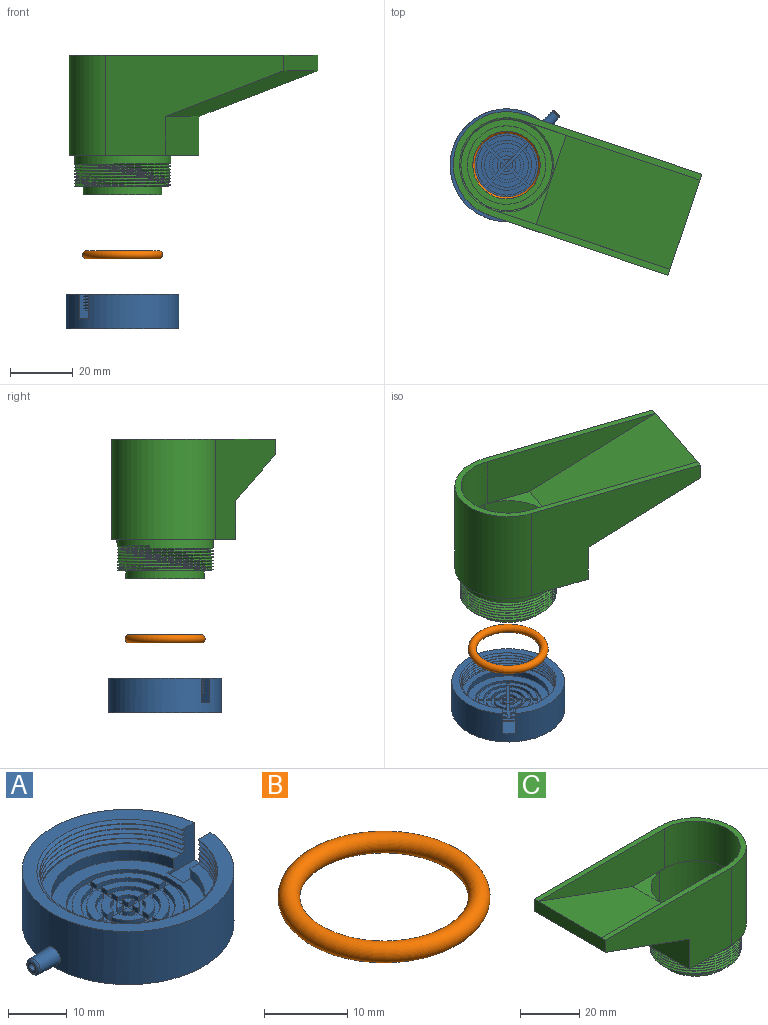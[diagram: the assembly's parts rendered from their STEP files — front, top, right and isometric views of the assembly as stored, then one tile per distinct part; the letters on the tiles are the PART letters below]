
ASSEMBLY  parts=3 mates=2
PART A: 117 faces, bbox 41.6x37.1x12.2 mm
  f0: cylinder r=18mm len=36mm, axis (0,0,1), area 1204.3mm2, adj f19,f69,f106,f113,f114,f115
  f1: cylinder r=15mm len=30mm, axis (0,0,1), area 16.3mm2, adj f16,f17,f20,f70,f113,f114
  f2: cylinder r=15mm len=30mm, axis (0,0,1), area 9mm2, adj f11,f15,f113,f114
  f3: cylinder r=15mm len=30mm, axis (0,0,1), area 9mm2, adj f10,f14,f113,f114
  f4: cylinder r=15mm len=30mm, axis (0,0,1), area 9mm2, adj f9,f13,f113,f114
  f5: cylinder r=15mm len=30mm, axis (0,0,1), area 9mm2, adj f8,f12,f113,f114
  f6: cylinder r=15mm len=6.76mm, axis (0,0,1), area 0.3mm2, adj f7,f19,f113
  f7: bspline ~31.89x31.56mm, area 26.7mm2, adj f6,f12,f19,f113
  f8: bspline ~36.44x31.56mm, area 83.4mm2, adj f5,f13,f113,f114
  f9: bspline ~36.44x31.56mm, area 83.4mm2, adj f4,f14,f113,f114
  f10: bspline ~36.44x31.56mm, area 83.4mm2, adj f3,f15,f113,f114
  f11: bspline ~36.44x31.56mm, area 83.4mm2, adj f2,f16,f113,f114
  f12: bspline ~36.44x31.56mm, area 65.4mm2, adj f5,f7,f19,f113,f114
  f13: bspline ~36.44x31.56mm, area 83.4mm2, adj f4,f8,f113,f114
  f14: bspline ~36.44x31.56mm, area 83.4mm2, adj f3,f9,f113,f114
  f15: bspline ~36.44x31.56mm, area 83.4mm2, adj f2,f10,f113,f114
  f16: bspline ~36.44x31.56mm, area 83.4mm2, adj f1,f11,f113,f114
  f17: plane 30x29.87mm, normal (0,0,1), area 167.9mm2, adj f1,f18,f71,f113,f114
  f18: cone r=13mm half-angle=5deg, axis (0,0,-1), area 172.9mm2, adj f17,f72,f113,f114
  f19: plane 36.65x36.53mm, normal (0,0,1), area 265.4mm2, adj f0,f6,f7,f12,f113,f114
  f20: bspline ~31.89x31.56mm, area 41.7mm2, adj f1,f21,f70,f114
  f21: bspline ~31.56x18.22mm, area 41.7mm2, adj f20,f70,f71,f114
  f22: cylinder r=18mm len=0.17mm, axis (0,0,1), area 0mm2, adj f95,f101,f111
  f23: cylinder r=18mm len=0.17mm, axis (0,0,1), area 0mm2, adj f96,f101,f111
  f24: cylinder r=18mm len=0.17mm, axis (0,0,1), area 0mm2, adj f96,f102,f111
  f25: plane 21x20.99mm, normal (0,0,1), area 171mm2, adj f26,f27,f28,f29,f34,f35,f36,f37
  f26: cylinder r=9.5mm len=8.99mm, axis (0,0,-1), area 13.9mm2, adj f25,f30,f94,f99
  f27: cylinder r=9.5mm len=8.99mm, axis (0,0,-1), area 13.9mm2, adj f25,f31,f95,f98
  f28: cylinder r=9.5mm len=8.99mm, axis (0,0,-1), area 13.9mm2, adj f25,f32,f93,f96
  f29: cylinder r=9.5mm len=8.99mm, axis (0,0,-1), area 13.9mm2, adj f25,f33,f97,f100
  f30: plane 8.99x8.99mm, normal (0,0,1), area 19.1mm2, adj f26,f34,f94,f99
  f31: plane 8.99x8.99mm, normal (0,0,1), area 19.1mm2, adj f27,f35,f95,f98
  f32: plane 8.99x8.99mm, normal (0,0,1), area 19.1mm2, adj f28,f36,f93,f96
  f33: plane 8.99x8.99mm, normal (0,0,1), area 19.1mm2, adj f29,f37,f97,f100
  f34: cylinder r=8mm len=7.48mm, axis (0,0,-1), area 11.6mm2, adj f25,f30,f94,f99
  f35: cylinder r=8mm len=7.48mm, axis (0,0,-1), area 11.6mm2, adj f25,f31,f95,f98
  f36: cylinder r=8mm len=7.48mm, axis (0,0,-1), area 11.6mm2, adj f25,f32,f93,f96
  f37: cylinder r=8mm len=7.48mm, axis (0,0,-1), area 11.6mm2, adj f25,f33,f97,f100
  f38: cylinder r=7mm len=6.48mm, axis (0,0,-1), area 10mm2, adj f25,f42,f88,f91
  f39: cylinder r=7mm len=6.48mm, axis (0,0,-1), area 10mm2, adj f25,f43,f90,f95
  f40: cylinder r=7mm len=6.48mm, axis (0,0,-1), area 10mm2, adj f25,f44,f87,f96
  f41: cylinder r=7mm len=6.48mm, axis (0,0,-1), area 10mm2, adj f25,f45,f89,f92
  f42: plane 6.48x6.48mm, normal (0,0,1), area 13.2mm2, adj f38,f46,f88,f91
  f43: plane 6.48x6.48mm, normal (0,0,1), area 13.2mm2, adj f39,f47,f90,f95
  f44: plane 6.48x6.48mm, normal (0,0,1), area 13.2mm2, adj f40,f48,f87,f96
  f45: plane 6.48x6.48mm, normal (0,0,1), area 13.2mm2, adj f41,f49,f89,f92
  f46: cylinder r=5.5mm len=4.98mm, axis (0,0,-1), area 7.6mm2, adj f25,f42,f88,f91
  f47: cylinder r=5.5mm len=4.98mm, axis (0,0,-1), area 7.6mm2, adj f25,f43,f90,f95
  f48: cylinder r=5.5mm len=4.98mm, axis (0,0,-1), area 7.6mm2, adj f25,f44,f87,f96
  f49: cylinder r=5.5mm len=4.98mm, axis (0,0,-1), area 7.6mm2, adj f25,f45,f89,f92
  f50: cylinder r=4.5mm len=3.97mm, axis (0,0,-1), area 6.1mm2, adj f25,f54,f76,f79
  f51: cylinder r=4.5mm len=3.97mm, axis (0,0,-1), area 6.1mm2, adj f25,f55,f78,f95
  f52: cylinder r=4.5mm len=3.97mm, axis (0,0,-1), area 6.1mm2, adj f25,f56,f75,f96
  f53: cylinder r=4.5mm len=3.97mm, axis (0,0,-1), area 6.1mm2, adj f25,f57,f77,f80
  f54: plane 3.97x3.97mm, normal (0,0,1), area 7.3mm2, adj f50,f62,f76,f79
  f55: plane 3.97x3.97mm, normal (0,0,1), area 7.3mm2, adj f51,f63,f78,f95
  f56: plane 3.97x3.97mm, normal (0,0,1), area 7.3mm2, adj f52,f64,f75,f96
  f57: plane 3.97x3.97mm, normal (0,0,1), area 7.3mm2, adj f53,f65,f77,f80
  f58: cylinder r=2mm len=1.44mm, axis (0,0,-1), area 2.1mm2, adj f25,f68,f85,f86
  f59: cylinder r=2mm len=1.44mm, axis (0,0,-1), area 2.1mm2, adj f25,f66,f83,f95
  f60: cylinder r=2mm len=1.44mm, axis (0,0,-1), area 2.1mm2, adj f25,f67,f84,f96
  f61: cylinder r=2mm len=1.44mm, axis (0,0,-1), area 2.1mm2, adj f25,f74,f81,f82
  f62: cylinder r=3mm len=2.46mm, axis (0,0,-1), area 3.7mm2, adj f25,f54,f76,f79
  f63: cylinder r=3mm len=2.46mm, axis (0,0,-1), area 3.7mm2, adj f25,f55,f78,f95
  f64: cylinder r=3mm len=2.46mm, axis (0,0,-1), area 3.7mm2, adj f25,f56,f75,f96
  f65: cylinder r=3mm len=2.46mm, axis (0,0,-1), area 3.7mm2, adj f25,f57,f77,f80
  f66: plane 1.44x1.44mm, normal (0,0,1), area 1.4mm2, adj f59,f83,f95
  f67: plane 1.44x1.44mm, normal (0,0,1), area 1.4mm2, adj f60,f84,f96
  f68: plane 1.44x1.44mm, normal (0,0,1), area 1.4mm2, adj f58,f85,f86
  f69: plane 36x36mm, normal (0,0,-1), area 1017.9mm2, adj f0
  f70: plane 0.9x0.78mm, normal (0,-1,0), area 0.4mm2, adj f1,f20,f21,f71
  f71: cylinder r=15mm len=29.87mm, axis (0,0,-1), area 11.8mm2, adj f17,f21,f70,f114
  f72: plane 26.39x26.23mm, normal (0,0,1), area 193.2mm2, adj f18,f73,f113,f114,f116
  f73: cylinder r=10.5mm len=21mm, axis (0,0,-1), area 66mm2, adj f25,f72,f102
  f74: plane 1.44x1.44mm, normal (0,0,1), area 1.4mm2, adj f61,f81,f82
  f75: plane 1.51x1mm, normal (1,0,0), area 1.5mm2, adj f25,f52,f56,f64
  f76: plane 1.51x1mm, normal (-1,0,0), area 1.5mm2, adj f25,f50,f54,f62
  f77: plane 1.51x1mm, normal (-1,0,0), area 1.5mm2, adj f25,f53,f57,f65
  f78: plane 1.51x1mm, normal (1,0,0), area 1.5mm2, adj f25,f51,f55,f63
  f79: plane 1.51x1mm, normal (0,1,0), area 1.5mm2, adj f25,f50,f54,f62
  f80: plane 1.51x1mm, normal (0,-1,0), area 1.5mm2, adj f25,f53,f57,f65
  f81: plane 1.44x1mm, normal (-1,0,0), area 1.4mm2, adj f25,f61,f74,f82
  f82: plane 1.44x1mm, normal (0,-1,0), area 1.4mm2, adj f25,f61,f74,f81
  f83: plane 1.44x1mm, normal (1,0,0), area 1.4mm2, adj f25,f59,f66,f95
  f84: plane 1.44x1mm, normal (1,0,0), area 1.4mm2, adj f25,f60,f67,f96
  f85: plane 1.44x1mm, normal (-1,0,0), area 1.4mm2, adj f25,f58,f68,f86
  f86: plane 1.44x1mm, normal (0,1,0), area 1.4mm2, adj f25,f58,f68,f85
  f87: plane 1.51x1mm, normal (1,0,0), area 1.5mm2, adj f25,f40,f44,f48
  f88: plane 1.51x1mm, normal (-1,0,0), area 1.5mm2, adj f25,f38,f42,f46
  f89: plane 1.51x1mm, normal (-1,0,0), area 1.5mm2, adj f25,f41,f45,f49
  f90: plane 1.51x1mm, normal (1,0,0), area 1.5mm2, adj f25,f39,f43,f47
  f91: plane 1.51x1mm, normal (0,1,0), area 1.5mm2, adj f25,f38,f42,f46
  f92: plane 1.51x1mm, normal (0,-1,0), area 1.5mm2, adj f25,f41,f45,f49
  f93: plane 1.5x1mm, normal (1,0,0), area 1.5mm2, adj f25,f28,f32,f36
  f94: plane 1.5x1mm, normal (-1,0,0), area 1.5mm2, adj f25,f26,f30,f34
  f95: plane 18.49x2mm, normal (0,-1,0), area 19mm2, adj f22,f25,f27,f31,f35,f39,f43,f47
  f96: plane 18.49x2mm, normal (0,1,0), area 19mm2, adj f23,f24,f25,f28,f32,f36,f40,f44
  f97: plane 1.5x1mm, normal (-1,0,0), area 1.5mm2, adj f25,f29,f33,f37
  f98: plane 1.5x1mm, normal (1,0,0), area 1.5mm2, adj f25,f27,f31,f35
  f99: plane 1.5x1mm, normal (0,1,0), area 1.5mm2, adj f25,f26,f30,f34
  f100: plane 1.5x1mm, normal (0,-1,0), area 1.5mm2, adj f25,f29,f33,f37
  f101: plane 7.55x1mm, normal (0,0,1), area 7.5mm2, adj f22,f23,f95,f96,f103,f108
  f102: plane 7.51x1mm, normal (0,0,-1), area 7.5mm2, adj f24,f73,f95,f96,f104,f110
  f103: plane 10.95x1mm, normal (-0.09,0,1), area 11mm2, adj f25,f95,f96,f101
  f104: cylinder r=18mm len=0.17mm, axis (0,0,1), area 0mm2, adj f95,f102,f111
  f105: plane 2.23x2.23mm, normal (-1,0,0), area 2.8mm2, adj f111,f112
  f106: cone r=1.5mm half-angle=2deg, axis (1,0,0), area 46.2mm2, adj f0,f112
  f107: cylinder r=18mm len=0.66mm, axis (0,0,1), area 0mm2, adj f96,f111
  f108: cylinder r=18mm len=0.66mm, axis (0,0,1), area 0mm2, adj f101,f111
  f109: cylinder r=18mm len=0.66mm, axis (0,0,1), area 0mm2, adj f95,f111
  f110: cylinder r=18mm len=0.66mm, axis (0,0,1), area 0mm2, adj f102,f111
  f111: cylinder r=0.6mm len=5.01mm, axis (-1,0,0), area 18.9mm2, adj f22,f23,f24,f104,f105,f107,f108,f109
  f112: torus R=1.11mm, axis (1,0,0), area 5.3mm2, adj f105,f106
  f113: plane 7.7x6.55mm, normal (0,-1,0), area 27.5mm2, adj f0,f1,f2,f3,f4,f5,f6,f7
  f114: plane 7.7x6.55mm, normal (0,1,0), area 27.5mm2, adj f0,f1,f2,f3,f4,f5,f8,f9
  f115: plane 6.65x4mm, normal (0,0,1), area 26.5mm2, adj f0,f113,f114,f116
  f116: plane 4x0.5mm, normal (1,0,0), area 2mm2, adj f72,f113,f114,f115
PART B: 1 faces, bbox 27.6x27.6x2.6 mm
  f0: torus R=11.46mm, axis (0,0,1), area 591.6mm2
PART C: 32 faces, bbox 77.7x36.1x45.2 mm
  f0: plane 60x32mm, normal (0,1,0), area 1131.2mm2, adj f1,f12,f13,f15,f30,f31
  f1: plane 37x34mm, normal (0,0,-1), area 393.7mm2, adj f0,f2,f14,f15,f31
  f2: cylinder r=15.35mm len=30.7mm, axis (0,0,1), area 241.1mm2, adj f1,f3,f25,f26
  f3: cylinder r=15.35mm len=30.7mm, axis (0,0,1), area 9.7mm2, adj f2,f4,f26,f27
  f4: cylinder r=15.35mm len=30.7mm, axis (0,0,1), area 9.7mm2, adj f3,f5,f26,f27
  f5: cylinder r=15.35mm len=30.7mm, axis (0,0,1), area 9.6mm2, adj f4,f6,f26,f27
  f6: cylinder r=15.35mm len=30.7mm, axis (0,0,1), area 9.7mm2, adj f5,f7,f26,f27
  f7: cylinder r=15.35mm len=30.7mm, axis (0,0,1), area 9.7mm2, adj f6,f8,f26,f27
  f8: cylinder r=15.35mm len=30.7mm, axis (0,0,1), area 9.7mm2, adj f7,f9,f26,f27
  f9: cylinder r=15.35mm len=30.7mm, axis (0,0,1), area 9.6mm2, adj f8,f10,f26,f27
  f10: cylinder r=15.35mm len=8.97mm, axis (0,0,1), area 0.5mm2, adj f9,f16,f27
  f11: plane 15x15mm, normal (0,0,1), area 48.3mm2, adj f17,f18,f22
  f12: plane 77x34mm, normal (0,0,1), area 340.5mm2, adj f0,f13,f14,f15,f18,f19,f20
  f13: plane 34x5mm, normal (-1,0,0), area 170mm2, adj f0,f12,f14,f17,f30
  f14: plane 60x32mm, normal (0,-1,0), area 1131.2mm2, adj f1,f12,f13,f15,f30,f31
  f15: cylinder r=17mm len=34mm, axis (0,0,-1), area 1709mm2, adj f0,f1,f12,f14
  f16: plane 30.71x30.71mm, normal (0,0,-1), area 216.1mm2, adj f10,f26,f27,f28
  f17: plane 45x30mm, normal (0.34,0,0.94), area 1436.6mm2, adj f11,f13,f18,f19,f21
  f18: plane 60x16.38mm, normal (0,-1,0), area 614.2mm2, adj f11,f12,f17,f20
  f19: plane 60x16.38mm, normal (0,1,0), area 614.2mm2, adj f12,f17,f20,f21
  f20: cylinder r=15mm len=30mm, axis (0,0,1), area 771.8mm2, adj f12,f18,f19,f22
  f21: plane 15x15mm, normal (0,0,1), area 48.3mm2, adj f17,f19,f22
  f22: cone r=15mm half-angle=15.2deg, axis (0,0,1), area 1309.6mm2, adj f11,f20,f21,f23
  f23: plane 21.5x21.5mm, normal (0,0,1), area 0mm2, adj f22,f24
  f24: cylinder r=10.75mm len=21.5mm, axis (0,0,-1), area 844.3mm2, adj f23,f29
  f25: plane 0.9x0.78mm, normal (0,-1,0), area 0.4mm2, adj f2,f26,f27
  f26: bspline ~35.45x30.7mm, area 658mm2, adj f2,f3,f4,f5,f6,f7,f8,f9
  f27: bspline ~35.45x30.7mm, area 622mm2, adj f3,f4,f5,f6,f7,f8,f9,f10
  f28: cylinder r=12.5mm len=25mm, axis (0,0,1), area 196.3mm2, adj f16,f29
  f29: plane 25x25mm, normal (0,0,-1), area 127.8mm2, adj f24,f28
  f30: plane 40x34mm, normal (-0.34,0,-0.94), area 1447.3mm2, adj f0,f13,f14,f31
  f31: plane 34x12.44mm, normal (-1,0,0), area 423mm2, adj f0,f1,f14,f30
PLACE A rot(axis=(0,0,-1),134deg) t=(3.35,10.01,-46.39)mm
PLACE B rot(axis=(0,0,-1),134deg) t=(3.35,10.01,-38.78)mm
PLACE C rot(axis=(0,0,1),161.5deg) t=(20.56,20.07,-7.07)mm
MATE cylindrical A.f0 <-> C.f2  axis (0,0,1) through (3.35,10.01,-56.89)mm
MATE slider B.f0 <-> A.f0  axis (0,0,1) through (3.35,10.01,-38.78)mm
